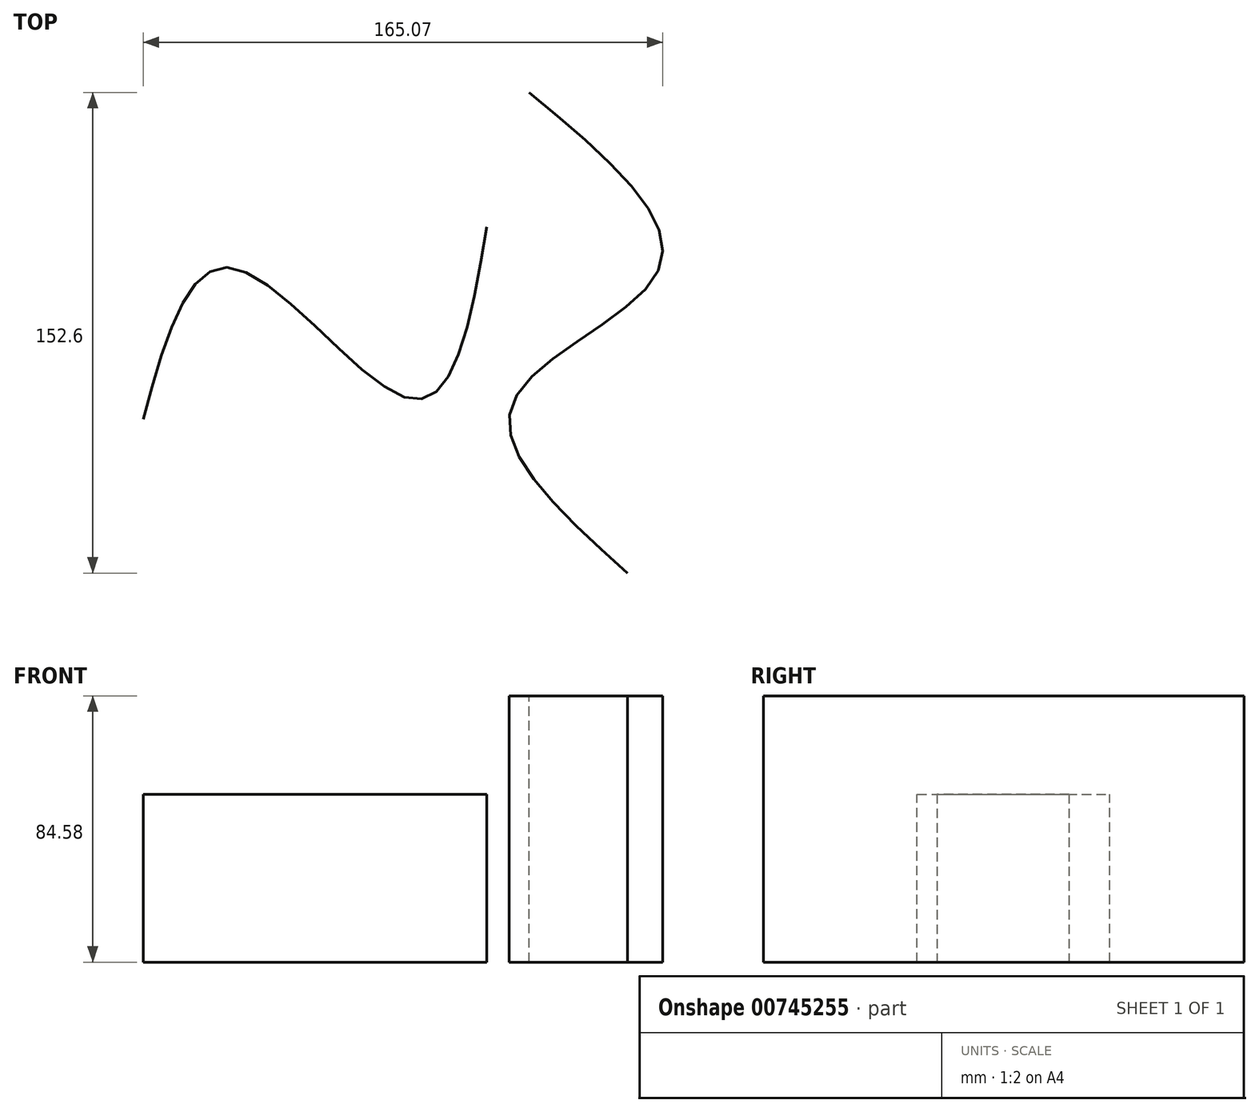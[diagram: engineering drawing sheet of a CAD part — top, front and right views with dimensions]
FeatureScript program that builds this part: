
annotation { "Feature Type Name" : "Feature", "Feature Type Description" : "" }
export const myFeature = defineFeature(function(context is Context, id is Id, definition is map)
    precondition{}
    {
        {
            var Q0;
            Q0=qCreatedBy(makeId("Top.planeOp"),FACE);
            var sketch = newSketch(context, id + "F0", { "sketchPlane" : qUnion([Q0])});
            skFitSpline(sketch, "E0", {"points": [v(-63.5, -48.13) * mm, v(-35.3, 0) * mm, v(22.26, -41.73) * mm, v(45.67, 13.06) * mm], "startDerivative": vector(65.1, 238.84) * mm, "endDerivative": vector(43.7, 259.05) * mm});
            skSolve(sketch);
        }
        {
            var Q0;
            Q0=sQuery(id+"F0.wireOp",EDGE,"E0");
            extrude(context, id + "F1", {"bodyType" : ToolBodyType.SURFACE, "surfaceEntities" : qUnion([Q0]), "depth" : 53.34 * mm, "offsetDistance" : 25.4 * mm});
        }
        {
            var Q0;
            Q0=qCreatedBy(makeId("Top.planeOp"),FACE);
            var sketch = newSketch(context, id + "F2", { "sketchPlane" : qUnion([Q0])});
            skFitSpline(sketch, "E1", {"points": [v(59.12, 55.7) * mm, v(100.51, 0) * mm, v(54, -42.68) * mm, v(90.35, -96.9) * mm], "startDerivative": vector(209.84, -173.77) * mm, "endDerivative": vector(194.53, -174.33) * mm});
            skSolve(sketch);
        }
        {
            var Q0;
            Q0=sQuery(id+"F2.wireOp",EDGE,"E1");
            extrude(context, id + "F3", {"bodyType" : ToolBodyType.SURFACE, "surfaceEntities" : qUnion([Q0]), "depth" : 84.58 * mm, "offsetDistance" : 25.4 * mm});
        }
    });
